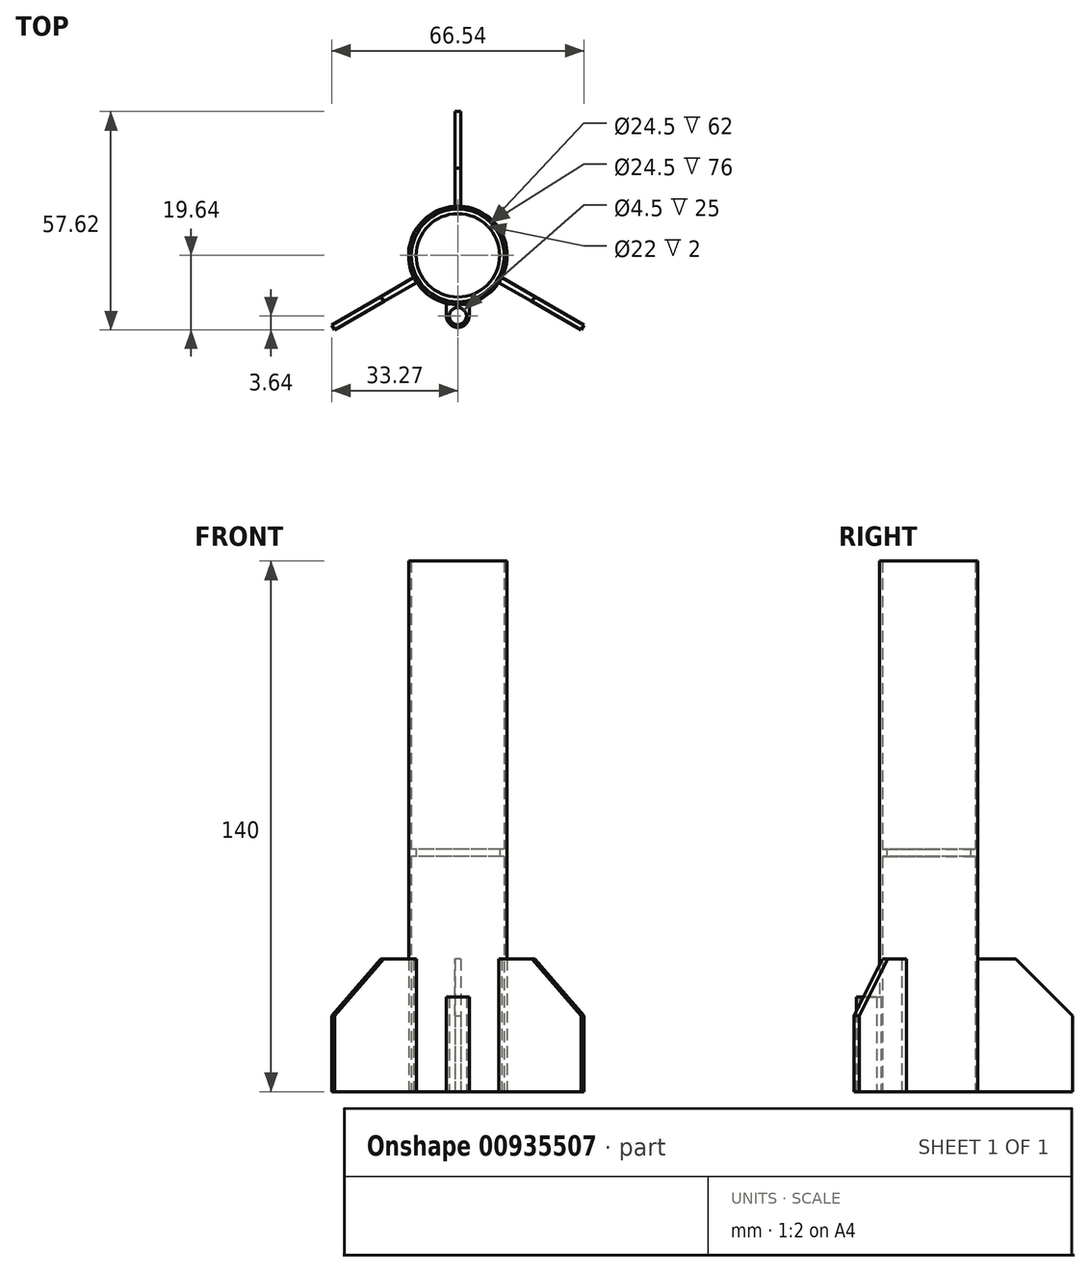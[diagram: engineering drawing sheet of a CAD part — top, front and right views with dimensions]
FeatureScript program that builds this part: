
annotation { "Feature Type Name" : "Feature", "Feature Type Description" : "" }
export const myFeature = defineFeature(function(context is Context, id is Id, definition is map)
    precondition{}
    {
        {
            var Q0;
            Q0=qCreatedBy(makeId("Top.planeOp"),FACE);
            var sketch = newSketch(context, id + "F0", { "sketchPlane" : qUnion([Q0])});
            skCircle(sketch, "E0", {"center": v(0, 0) * mm, "radius": 12.25 * mm});
            skCircle(sketch, "E1", {"center": v(0, 0) * mm, "radius": 13 * mm});
            skCircle(sketch, "E2", {"center": v(0, -16) * mm, "radius": 2.25 * mm});
            skCircle(sketch, "E3", {"center": v(0, -16) * mm, "radius": 3 * mm});
            skLineSegment(sketch, "E4", {"start": v(-3, -16) * mm, "end": v(-3, -12.65) * mm});
            skLineSegment(sketch, "E5", {"start": v(3, -16) * mm, "end": v(3, -12.65) * mm});
            skLineSegment(sketch, "E6.bottom", {"start": v(-0.75, 37.98) * mm, "end": v(0.75, 37.98) * mm});
            skLineSegment(sketch, "E6.top", {"start": v(-0.75, 12.98) * mm, "end": v(0.75, 12.98) * mm, "construction": true});
            skLineSegment(sketch, "E6.left", {"start": v(-0.75, 37.98) * mm, "end": v(-0.75, 12.98) * mm});
            skLineSegment(sketch, "E6.right", {"start": v(0.75, 37.98) * mm, "end": v(0.75, 12.98) * mm});
            skCircle(sketch, "E7", {"center": v(0, 0) * mm, "radius": 11 * mm});
            skSolve(sketch);
        }
        {
            var Q0;
            Q0=makeQuery(id+"F0.imprint","IMPRINT",FACE,{"disambiguationData":[TD([[makeQuery(id+"F0.imprint","IMPRINT",EDGE,{"derivedFrom":sQuery(id+"F0.wireOp",EDGE,"E0")}),-1.0]])]});
            extrude(context, id + "F1", {"entities" : qUnion([Q0]), "depth" : 140 * mm, "offsetDistance" : 25 * mm});
        }
        {
            var Q0;
            Q0=makeQuery(id+"F0.imprint","IMPRINT",FACE,{"disambiguationData":[TD([[makeQuery(id+"F0.imprint","IMPRINT",EDGE,{"derivedFrom":sQuery(id+"F0.wireOp",EDGE,"E6.bottom")}),-1.0]])]});
            extrude(context, id + "F2", {"entities" : qUnion([Q0]), "operationType" : NewBodyOperationType.ADD, "depth" : 35 * mm, "offsetDistance" : 25 * mm});
        }
        {
            var Q0;
            Q0=makeQuery(id+"F2.opExtrude","CAP_EDGE",EDGE,{"disambiguationData":[OSD([sQuery(id+"F0.wireOp",EDGE,"E6.bottom")])],"isStart":false});
            chamfer(context, id + "F3", {"entities" : qUnion([Q0]), "width" : 15 * mm, "tangentPropagation" : true});
        }
        {
            var Q0;
            Q0=makeQuery(id+"F1.opExtrude","SWEPT_BODY",BODY,{"disambiguationData":[OSD([sQuery(id+"F0.wireOp",EDGE,"E0"),sQuery(id+"F0.wireOp",EDGE,"E1")])]});
            var Q1;
            Q1=makeQuery(id+"F1.opExtrude","CAP_EDGE",EDGE,{"disambiguationData":[OSD([sQuery(id+"F0.wireOp",EDGE,"E0")])],"isStart":false});
            circularPattern(context, id + "F4", {"entities" : qUnion([Q0]), "axis" : qUnion([Q1]), "angle" : 360 * degree, "instanceCount" : 3, "equalSpace" : true});
        }
        {
            var Q0;
            Q0=makeQuery(id+"F0.imprint","IMPRINT",FACE,{"disambiguationData":[TD([[makeQuery(id+"F0.imprint","IMPRINT",EDGE,{"derivedFrom":sQuery(id+"F0.wireOp",EDGE,"E2")}),-1.0]])]});
            var Q1;
            {var subQ0=sQuery(id+"F0.wireOp",EDGE,"E5");Q1=makeQuery(id+"F0.imprint","IMPRINT",FACE,{"disambiguationData":[TD([[makeQuery(id+"F0.imprint","IMPRINT",EDGE,{"derivedFrom":subQ0}),1.0]])]});}
            var Q2;
            {var subQ0=sQuery(id+"F0.wireOp",EDGE,"E4");Q2=makeQuery(id+"F0.imprint","IMPRINT",FACE,{"disambiguationData":[TD([[makeQuery(id+"F0.imprint","IMPRINT",EDGE,{"derivedFrom":subQ0}),-1.0]])]});}
            extrude(context, id + "F5", {"entities" : qUnion([Q0, Q1, Q2]), "operationType" : NewBodyOperationType.ADD, "depth" : 25 * mm, "offsetDistance" : 25 * mm});
        }
        {
            var Q0;
            Q0=makeQuery(id+"F0.imprint","IMPRINT",FACE,{"disambiguationData":[TD([[makeQuery(id+"F0.imprint","IMPRINT",EDGE,{"derivedFrom":sQuery(id+"F0.wireOp",EDGE,"E0")}),1.0]])]});
            extrude(context, id + "F6", {"entities" : qUnion([Q0]), "operationType" : NewBodyOperationType.ADD, "depth" : 64 * mm, "offsetDistance" : 25 * mm, "hasSecondDirection" : true, "secondDirectionOppositeDirection" : false, "secondDirectionDepth" : 62 * mm});
        }
    });
